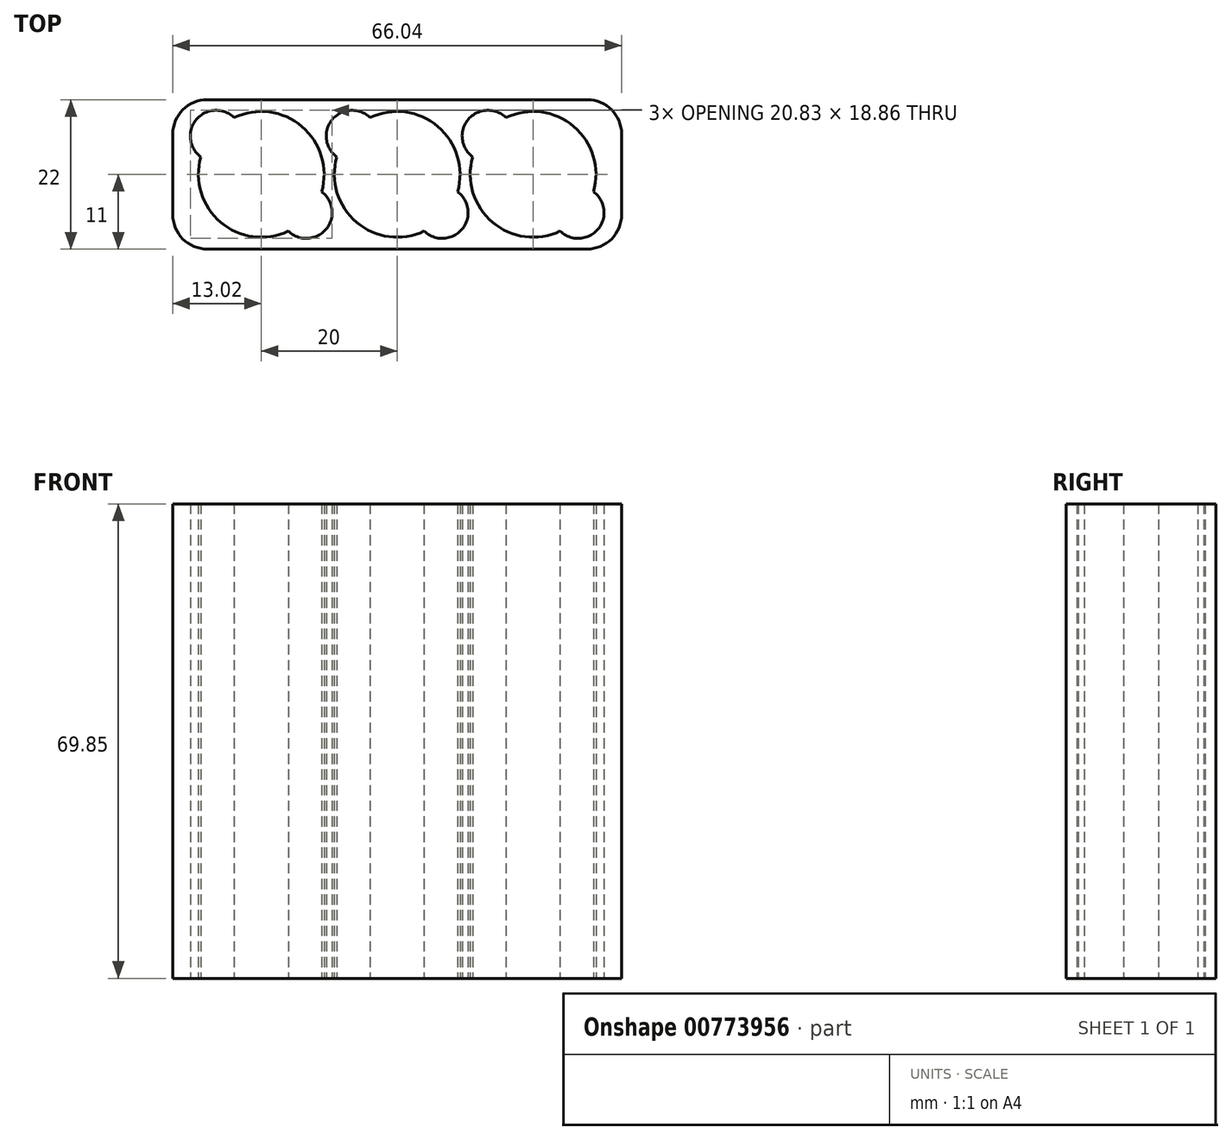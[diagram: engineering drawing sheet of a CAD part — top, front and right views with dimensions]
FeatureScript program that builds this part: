
annotation { "Feature Type Name" : "Feature", "Feature Type Description" : "" }
export const myFeature = defineFeature(function(context is Context, id is Id, definition is map)
    precondition{}
    {
        {
            var Q0;
            Q0=qCreatedBy(makeId("Top.planeOp"),FACE);
            var sketch = newSketch(context, id + "F0", { "sketchPlane" : qUnion([Q0])});
            skLineSegment(sketch, "E0.bottom", {"start": v(33.02, 11) * mm, "end": v(-33.02, 11) * mm});
            skLineSegment(sketch, "E0.top", {"start": v(33.02, -11) * mm, "end": v(-33.02, -11) * mm});
            skLineSegment(sketch, "E0.left", {"start": v(33.02, 11) * mm, "end": v(33.02, -11) * mm});
            skLineSegment(sketch, "E0.right", {"start": v(-33.02, 11) * mm, "end": v(-33.02, -11) * mm});
            skPoint(sketch, "E0.middle", {"position": v(0, 0) * mm});
            skArc(sketch, "E1", {"start": v(-8.9, 2.55) * mm, "mid": v(-5.98, -7.06) * mm, "end": v(3.97, -8.35) * mm});
            skPoint(sketch, "E2.start.orphan", {"position": v(0, -9.25) * mm});
            skArc(sketch, "E3", {"start": v(3.97, -8.35) * mm, "mid": v(9.54, -8.09) * mm, "end": v(8.9, -2.55) * mm});
            skArc(sketch, "E4.1.0", {"start": v(-3.97, 8.35) * mm, "mid": v(-9.54, 8.09) * mm, "end": v(-8.9, 2.55) * mm});
            skArc(sketch, "E5.trimOffspring", {"start": v(8.9, -2.55) * mm, "mid": v(5.98, 7.06) * mm, "end": v(-3.97, 8.35) * mm});
            skArc(sketch, "E6.1.0.0", {"start": v(28.9, -2.55) * mm, "mid": v(25.98, 7.06) * mm, "end": v(16.03, 8.35) * mm});
            skArc(sketch, "E6.1.0.1", {"start": v(11.1, 2.55) * mm, "mid": v(14.02, -7.06) * mm, "end": v(23.97, -8.35) * mm});
            skArc(sketch, "E6.1.0.2", {"start": v(16.03, 8.35) * mm, "mid": v(10.46, 8.09) * mm, "end": v(11.1, 2.55) * mm});
            skArc(sketch, "E6.1.0.3", {"start": v(23.97, -8.35) * mm, "mid": v(29.54, -8.09) * mm, "end": v(28.9, -2.55) * mm});
            skLineSegment(sketch, "E6.direction1", {"start": v(-8.9, 2.55) * mm, "end": v(11.1, 2.55) * mm, "construction": true});
            skLineSegment(sketch, "E7.direction1", {"start": v(-8.9, 2.55) * mm, "end": v(-28.9, 2.55) * mm, "construction": true});
            skArc(sketch, "E8.0.1.0", {"start": v(-11.1, -2.55) * mm, "mid": v(-14.02, 7.06) * mm, "end": v(-23.97, 8.35) * mm});
            skArc(sketch, "E8.4.1.0", {"start": v(-28.9, 2.55) * mm, "mid": v(-25.98, -7.06) * mm, "end": v(-16.03, -8.35) * mm});
            skArc(sketch, "E8.8.1.0", {"start": v(-23.97, 8.35) * mm, "mid": v(-29.54, 8.09) * mm, "end": v(-28.9, 2.55) * mm});
            skArc(sketch, "E8.12.1.0", {"start": v(-16.03, -8.35) * mm, "mid": v(-10.46, -8.09) * mm, "end": v(-11.1, -2.55) * mm});
            skSolve(sketch);
        }
        {
            var Q0;
            Q0=qSketchRegion(id+"F0",true);
            extrude(context, id + "F1", {"entities" : qUnion([Q0]), "depth" : 69.85 * mm, "offsetDistance" : 25.4 * mm});
        }
        {
            var Q0;
            Q0=makeQuery(id+"F1.opExtrude","SWEPT_EDGE",EDGE,{"disambiguationData":[OSD([sQuery(id+"F0.wireOp",EDGE,"E0.bottom"),sQuery(id+"F0.wireOp",EDGE,"E0.right")])]});
            var Q1;
            Q1=makeQuery(id+"F1.opExtrude","SWEPT_EDGE",EDGE,{"disambiguationData":[OSD([sQuery(id+"F0.wireOp",EDGE,"E0.top"),sQuery(id+"F0.wireOp",EDGE,"E0.right")])]});
            var Q2;
            Q2=makeQuery(id+"F1.opExtrude","SWEPT_EDGE",EDGE,{"disambiguationData":[OSD([sQuery(id+"F0.wireOp",EDGE,"E0.top"),sQuery(id+"F0.wireOp",EDGE,"E0.left")])]});
            var Q3;
            Q3=makeQuery(id+"F1.opExtrude","SWEPT_EDGE",EDGE,{"disambiguationData":[OSD([sQuery(id+"F0.wireOp",EDGE,"E0.bottom"),sQuery(id+"F0.wireOp",EDGE,"E0.left")])]});
            fillet(context, id + "F2", {"entities" : qUnion([Q0, Q1, Q2, Q3]), "radius" : 5.08 * mm, "tangentPropagation" : true, "allowEdgeOverflow" : false});
        }
    });
